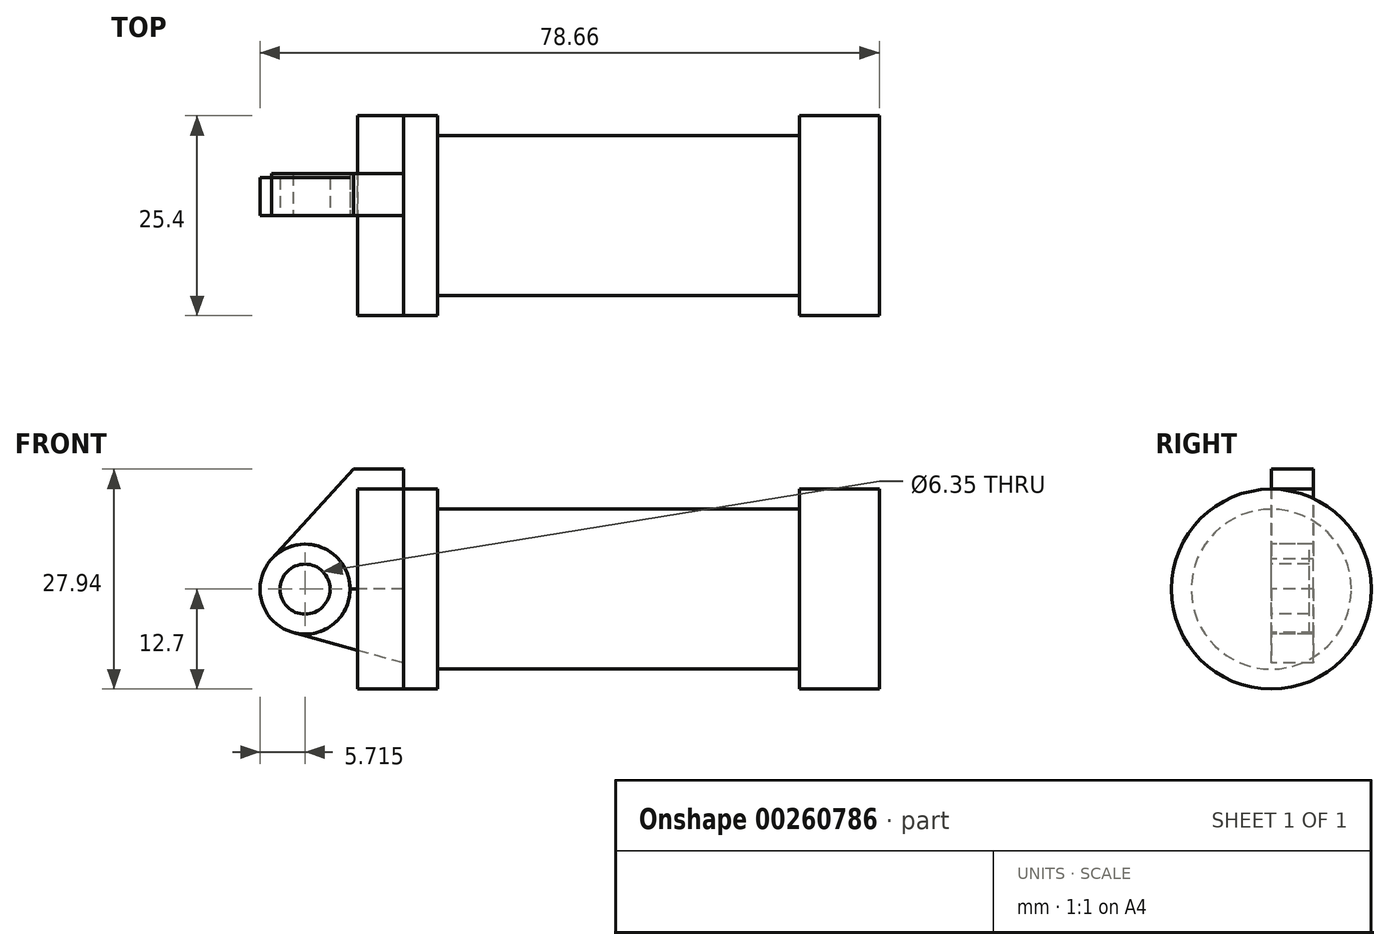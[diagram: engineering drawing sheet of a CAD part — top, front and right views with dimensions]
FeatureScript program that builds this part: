
annotation { "Feature Type Name" : "Feature", "Feature Type Description" : "" }
export const myFeature = defineFeature(function(context is Context, id is Id, definition is map)
    precondition{}
    {
        {
            var Q0;
            Q0=qCreatedBy(makeId("Front.planeOp"),FACE);
            var sketch = newSketch(context, id + "F0", { "sketchPlane" : qUnion([Q0])});
            skLineSegment(sketch, "E0", {"start": v(0, 0) * mm, "end": v(0, 12.7) * mm});
            skLineSegment(sketch, "E1", {"start": v(0, 12.7) * mm, "end": v(10.16, 12.7) * mm});
            skLineSegment(sketch, "E2", {"start": v(10.16, 12.7) * mm, "end": v(10.16, 10.16) * mm});
            skLineSegment(sketch, "E3", {"start": v(10.16, 10.16) * mm, "end": v(56.13, 10.16) * mm});
            skLineSegment(sketch, "E4", {"start": v(56.13, 10.16) * mm, "end": v(56.13, 12.7) * mm});
            skLineSegment(sketch, "E5", {"start": v(56.13, 12.7) * mm, "end": v(66.3, 12.7) * mm});
            skLineSegment(sketch, "E6", {"start": v(66.3, 12.7) * mm, "end": v(66.3, 0) * mm});
            skLineSegment(sketch, "E7", {"start": v(66.3, 0) * mm, "end": v(0, 0) * mm});
            skLineSegment(sketch, "E8", {"start": v(5.84, 15.24) * mm, "end": v(-0.5, 15.24) * mm});
            skLineSegment(sketch, "E9", {"start": v(-0.5, 15.24) * mm, "end": v(-10.88, 3.85) * mm});
            skLineSegment(sketch, "E10", {"start": v(0, 0) * mm, "end": v(-6.65, 0) * mm});
            skCircle(sketch, "E11", {"center": v(-6.65, 0) * mm, "radius": 5.72 * mm});
            skCircle(sketch, "E12", {"center": v(-6.65, 0) * mm, "radius": 3.18 * mm});
            skLineSegment(sketch, "E13", {"start": v(5.84, 15.24) * mm, "end": v(5.84, -9.4) * mm});
            skLineSegment(sketch, "E14", {"start": v(5.84, -9.4) * mm, "end": v(-8.18, -5.5) * mm});
            skSolve(sketch);
        }
        {
            var Q0;
            {var subQ0=sQuery(id+"F0.wireOp",EDGE,"E2");Q0=makeQuery(id+"F0.imprint","IMPRINT",FACE,{"disambiguationData":[TD([[makeQuery(id+"F0.imprint","IMPRINT",EDGE,{"derivedFrom":subQ0}),-1.0]])]});}
            var Q1;
            Q1=sQuery(id+"F0.wireOp",EDGE,"E7");
            revolve(context, id + "F1", {"entities" : qUnion([Q0]), "axis" : qUnion([Q1]), "revolveType" : RevolveType.FULL});
        }
        {
            var Q0;
            {var subQ3=sQuery(id+"F0.wireOp",EDGE,"E0");Q0=makeQuery(id+"F0.imprint","IMPRINT",FACE,{"disambiguationData":[TD([[makeQuery(id+"F0.imprint","IMPRINT",EDGE,{"derivedFrom":subQ3}),1.0]])]});}
            extrude(context, id + "F2", {"entities" : qUnion([Q0]), "oppositeDirection" : true, "depth" : 5.33 * mm});
        }
        {
            var Q0;
            Q0=makeQuery(id+"F1.opRevolve","SWEPT_FACE",FACE,{"disambiguationData":[OSD([sQuery(id+"F0.wireOp",EDGE,"E13")])]});
            extrude(context, id + "F3", {"entities" : qUnion([Q0]), "depth" : 5.84 * mm});
        }
        {
            var Q0;
            {var subQ0=sQuery(id+"F0.wireOp",EDGE,"E14");Q0=makeQuery(id+"F0.imprint","IMPRINT",FACE,{"disambiguationData":[TD([[makeQuery(id+"F0.imprint","IMPRINT",EDGE,{"derivedFrom":subQ0}),-1.0]])]});}
            extrude(context, id + "F4", {"entities" : qUnion([Q0]), "oppositeDirection" : true, "depth" : 5.33 * mm});
        }
        {
            var Q0;
            {var subQ4=sQuery(id+"F0.wireOp",EDGE,"E12");Q0=makeQuery(id+"F0.imprint","IMPRINT",FACE,{"disambiguationData":[TD([[makeQuery(id+"F0.imprint","IMPRINT",EDGE,{"derivedFrom":subQ4}),-1.0]])]});}
            extrude(context, id + "F5", {"entities" : qUnion([Q0]), "oppositeDirection" : true, "depth" : 4.83 * mm});
        }
    });
